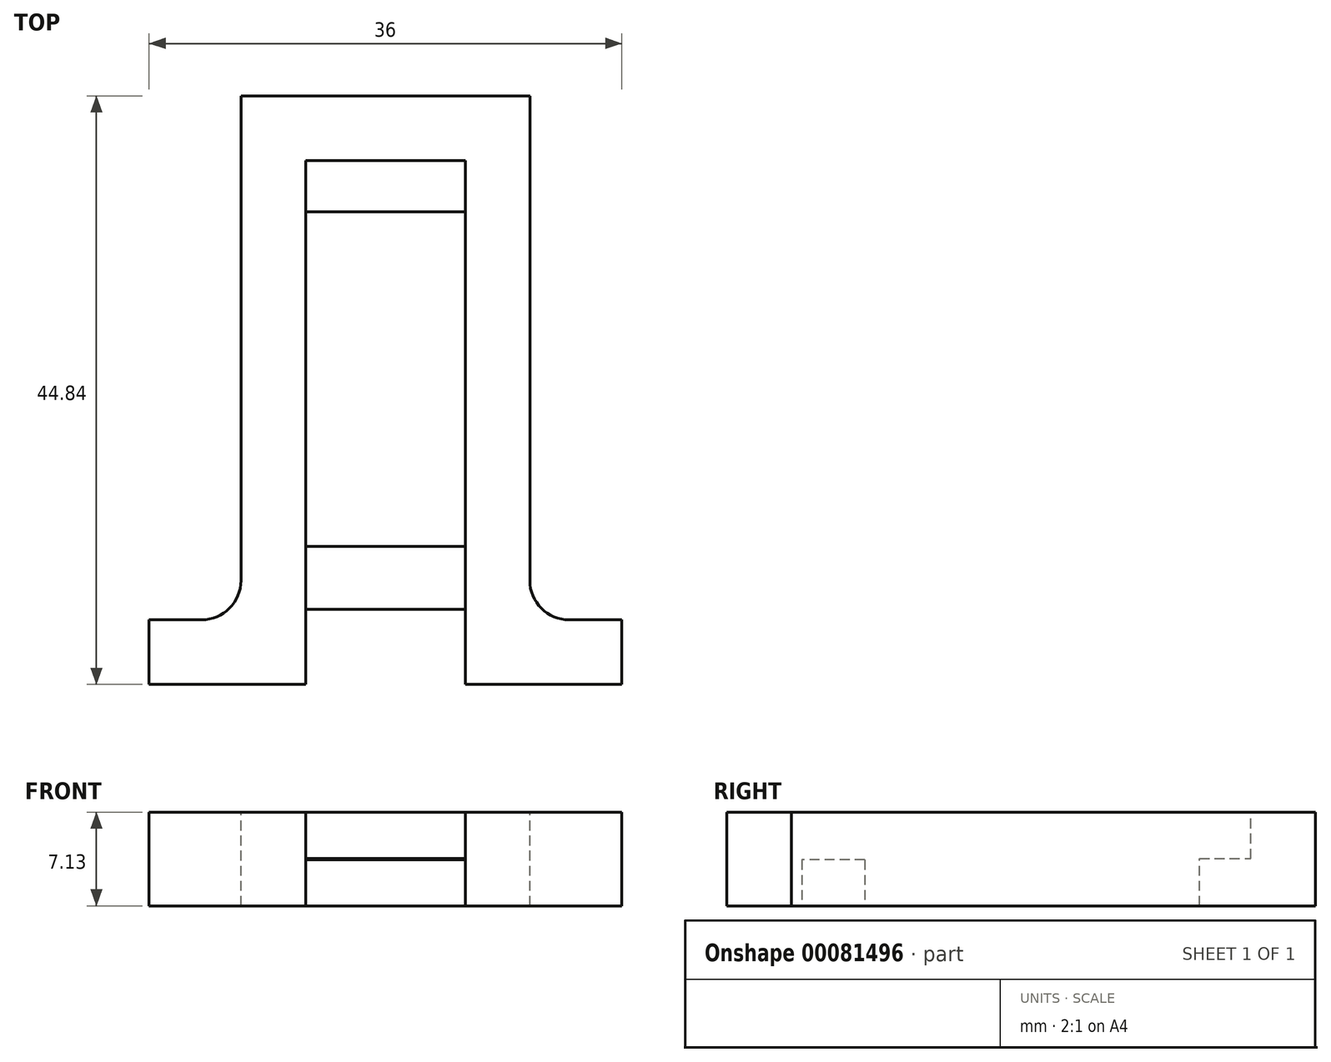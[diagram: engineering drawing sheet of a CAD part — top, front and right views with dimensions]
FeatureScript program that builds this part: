
annotation { "Feature Type Name" : "Feature", "Feature Type Description" : "" }
export const myFeature = defineFeature(function(context is Context, id is Id, definition is map)
    precondition{}
    {
        {
            var Q0;
            Q0=qCreatedBy(makeId("Top.planeOp"),FACE);
            var sketch = newSketch(context, id + "F0", { "sketchPlane" : qUnion([Q0])});
            skLineSegment(sketch, "E0.bottom", {"start": v(-15.59, 27.6) * mm, "end": v(20.41, 27.6) * mm});
            skLineSegment(sketch, "E0.top", {"start": v(-15.59, -17.24) * mm, "end": v(20.41, -17.24) * mm});
            skLineSegment(sketch, "E0.left", {"start": v(-15.59, 27.6) * mm, "end": v(-15.59, -17.24) * mm});
            skLineSegment(sketch, "E0.right", {"start": v(20.41, 27.6) * mm, "end": v(20.41, -17.24) * mm});
            skSolve(sketch);
        }
        {
            var Q0;
            Q0 = qSketchRegion(id + "F0", true);
            extrude(context, id + "F1", {"entities" : qUnion([Q0]), "depth" : 7.13 * mm});
        }
        {
            var Q0;
            Q0=makeQuery(id+"F1.opExtrude","CAP_FACE",FACE,{"disambiguationData":[OSD([sQuery(id+"F0.wireOp",EDGE,"E0.bottom"),sQuery(id+"F0.wireOp",EDGE,"E0.top"),sQuery(id+"F0.wireOp",EDGE,"E0.left"),sQuery(id+"F0.wireOp",EDGE,"E0.right")])],"isStart":false});
            var sketch = newSketch(context, id + "F2", { "sketchPlane" : qUnion([Q0])});
            skLineSegment(sketch, "E1.bottom", {"start": v(-15.59, 27.6) * mm, "end": v(-8.59, 27.6) * mm});
            skLineSegment(sketch, "E1.top", {"start": v(-15.59, -12.32) * mm, "end": v(-8.59, -12.32) * mm});
            skLineSegment(sketch, "E1.left", {"start": v(-15.59, 27.6) * mm, "end": v(-15.59, -12.32) * mm});
            skLineSegment(sketch, "E1.right", {"start": v(-8.59, 27.6) * mm, "end": v(-8.59, -12.32) * mm});
            skLineSegment(sketch, "E2.bottom", {"start": v(20.41, 27.6) * mm, "end": v(13.41, 27.6) * mm});
            skLineSegment(sketch, "E2.top", {"start": v(20.41, -12.32) * mm, "end": v(13.41, -12.32) * mm});
            skLineSegment(sketch, "E2.left", {"start": v(20.41, 27.6) * mm, "end": v(20.41, -12.32) * mm});
            skLineSegment(sketch, "E2.right", {"start": v(13.41, 27.6) * mm, "end": v(13.41, -12.32) * mm});
            skSolve(sketch);
        }
        {
            var Q0;
            Q0 = qSketchRegion(id + "F2", true);
            extrude(context, id + "F3", {"entities" : qUnion([Q0]), "operationType" : NewBodyOperationType.REMOVE, "oppositeDirection" : true, "depth" : 7.13 * mm});
        }
        {
            var Q0;
            Q0=makeQuery(id+"F1.opExtrude","CAP_FACE",FACE,{"disambiguationData":[OSD([sQuery(id+"F0.wireOp",EDGE,"E0.bottom"),sQuery(id+"F0.wireOp",EDGE,"E0.top"),sQuery(id+"F0.wireOp",EDGE,"E0.left"),sQuery(id+"F0.wireOp",EDGE,"E0.right")])],"isStart":false});
            var sketch = newSketch(context, id + "F4", { "sketchPlane" : qUnion([Q0])});
            skLineSegment(sketch, "E3.bottom", {"start": v(-3.67, 18.77) * mm, "end": v(8.5, 18.77) * mm});
            skLineSegment(sketch, "E3.top", {"start": v(-3.67, -17.24) * mm, "end": v(8.5, -17.24) * mm});
            skLineSegment(sketch, "E3.left", {"start": v(-3.67, 18.77) * mm, "end": v(-3.67, -17.24) * mm});
            skLineSegment(sketch, "E3.right", {"start": v(8.5, 18.77) * mm, "end": v(8.5, -17.24) * mm});
            skSolve(sketch);
        }
        {
            var Q0;
            Q0 = qSketchRegion(id + "F4", true);
            extrude(context, id + "F5", {"entities" : qUnion([Q0]), "operationType" : NewBodyOperationType.REMOVE, "oppositeDirection" : true, "depth" : 7.13 * mm});
        }
        {
            var Q0;
            Q0=makeQuery(id+"F1.opExtrude","CAP_FACE",FACE,{"disambiguationData":[OSD([sQuery(id+"F0.wireOp",EDGE,"E0.bottom"),sQuery(id+"F0.wireOp",EDGE,"E0.top"),sQuery(id+"F0.wireOp",EDGE,"E0.left"),sQuery(id+"F0.wireOp",EDGE,"E0.right")])],"isStart":false});
            var sketch = newSketch(context, id + "F6", { "sketchPlane" : qUnion([Q0])});
            skLineSegment(sketch, "E4.bottom", {"start": v(-3.67, 18.77) * mm, "end": v(8.5, 18.77) * mm});
            skLineSegment(sketch, "E4.top", {"start": v(-3.67, 22.68) * mm, "end": v(8.5, 22.68) * mm});
            skLineSegment(sketch, "E4.left", {"start": v(-3.67, 18.77) * mm, "end": v(-3.67, 22.68) * mm});
            skLineSegment(sketch, "E4.right", {"start": v(8.5, 18.77) * mm, "end": v(8.5, 22.68) * mm});
            skSolve(sketch);
        }
        {
            var Q0;
            Q0 = qSketchRegion(id + "F6", true);
            extrude(context, id + "F7", {"entities" : qUnion([Q0]), "operationType" : NewBodyOperationType.REMOVE, "oppositeDirection" : true, "depth" : 3.53 * mm});
        }
        {
            var Q0;
            Q0=makeQuery(id+"F1.opExtrude","CAP_FACE",FACE,{"disambiguationData":[OSD([sQuery(id+"F0.wireOp",EDGE,"E0.bottom"),sQuery(id+"F0.wireOp",EDGE,"E0.top"),sQuery(id+"F0.wireOp",EDGE,"E0.left"),sQuery(id+"F0.wireOp",EDGE,"E0.right")])],"isStart":true});
            var sketch = newSketch(context, id + "F8", { "sketchPlane" : qUnion([Q0])});
            skLineSegment(sketch, "E5.bottom", {"start": v(-3.67, 11.53) * mm, "end": v(8.5, 11.53) * mm});
            skLineSegment(sketch, "E5.top", {"start": v(-3.67, 6.73) * mm, "end": v(8.5, 6.73) * mm});
            skLineSegment(sketch, "E5.left", {"start": v(-3.67, 11.53) * mm, "end": v(-3.67, 6.73) * mm});
            skLineSegment(sketch, "E5.right", {"start": v(8.5, 11.53) * mm, "end": v(8.5, 6.73) * mm});
            skSolve(sketch);
        }
        {
            var Q0;
            Q0 = qSketchRegion(id + "F8", true);
            extrude(context, id + "F9", {"entities" : qUnion([Q0]), "operationType" : NewBodyOperationType.ADD, "oppositeDirection" : true, "depth" : 3.5 * mm});
        }
        {
            var Q0;
            Q0=makeQuery(id+"F3.boolean.opBoolean","COPY",EDGE,{"derivedFrom":makeQuery(id+"F3.opExtrude","SWEPT_EDGE",EDGE,{"disambiguationData":[OSD([sQuery(id+"F2.wireOp",EDGE,"E2.top"),sQuery(id+"F2.wireOp",EDGE,"E2.right")])]})});
            var Q1;
            Q1=makeQuery(id+"F3.boolean.opBoolean","COPY",EDGE,{"derivedFrom":makeQuery(id+"F3.opExtrude","SWEPT_EDGE",EDGE,{"disambiguationData":[OSD([sQuery(id+"F2.wireOp",EDGE,"E1.top"),sQuery(id+"F2.wireOp",EDGE,"E1.right")])]})});
            fillet(context, id + "F10", {"entities" : qUnion([Q0, Q1]), "radius" : 3 * mm, "tangentPropagation" : true, "allowEdgeOverflow" : false});
        }
    });
